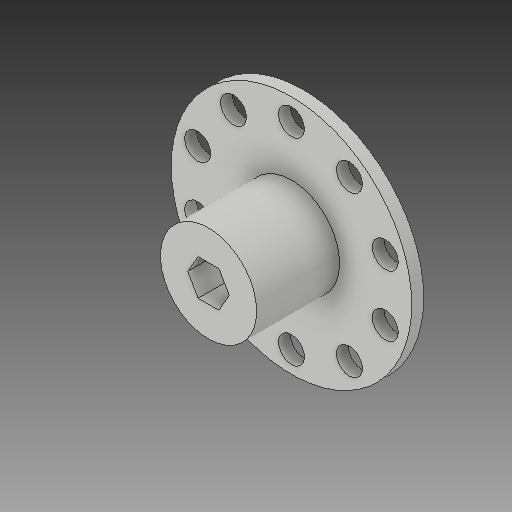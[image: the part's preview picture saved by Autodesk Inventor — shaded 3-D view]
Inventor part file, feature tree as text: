
AUTODESK INVENTOR PART (.ipt)
format: ipt  version: 2018 (Build 220112000, 112)  size: 166,400 bytes
history: native  units: in
note: dims shown in document units (in); Inventor stores cm internally (conversion verified against a paired STEP export)
features: extrude x2, sketch x2, projected_geometry x1
ambient origin geometry x8: Origin, YZ Plane, XZ Plane, XY Plane, X Axis, Y Axis, Z Axis, Center Point
bodies: Solid1 (feature_tree)
feature tree (5):
  extrude  "Extrusion1"  Depth=0.375in
  extrude  "Extrusion2"  Depth=0.125in TaperAngle=0.0deg
  sketch  "Sketch1"  dims[d0=0.27in d1=0.375in]
  sketch  "Sketch2"  dims[d2=3.937in d4=360.0deg d6=0.125in d7=0.0in d8=2.5in d9=1.0in d10=0.8625in d11=0.0in]
  projected_geometry  "Projected Loop1"
